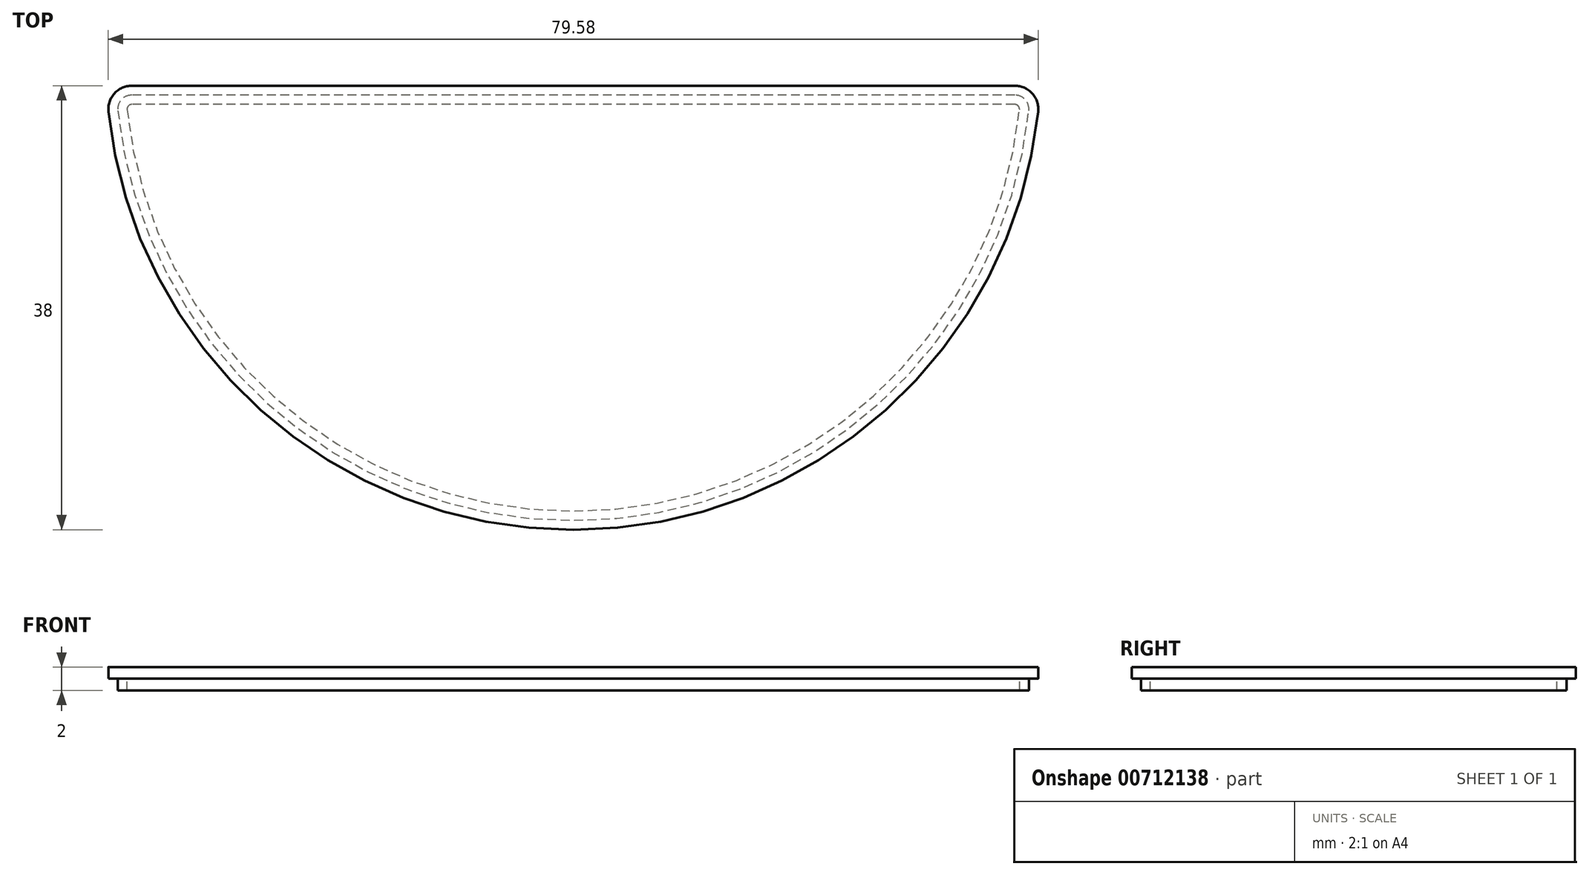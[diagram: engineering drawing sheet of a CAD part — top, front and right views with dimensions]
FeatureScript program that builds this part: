
annotation { "Feature Type Name" : "Feature", "Feature Type Description" : "" }
export const myFeature = defineFeature(function(context is Context, id is Id, definition is map)
    precondition{}
    {
        {
            var Q0;
            Q0=qCreatedBy(makeId("Top.planeOp"),FACE);
            var sketch = newSketch(context, id + "F0", { "sketchPlane" : qUnion([Q0])});
            skLineSegment(sketch, "E0.top", {"start": v(26.52, -2) * mm, "end": v(-49.06, -2) * mm});
            skPoint(sketch, "E1.visualSharp", {"position": v(28.68, -2) * mm});
            skArc(sketch, "E1.filletArc", {"start": v(28.5, -4.21) * mm, "mid": v(28, -2.66) * mm, "end": v(26.52, -2) * mm});
            skArc(sketch, "E2.1", {"start": v(27.71, -4.13) * mm, "mid": v(27.41, -3.2) * mm, "end": v(26.52, -2.8) * mm});
            skLineSegment(sketch, "E2.2", {"start": v(26.52, -2.8) * mm, "end": v(-49.06, -2.8) * mm});
            skArc(sketch, "E3", {"start": v(-51.05, -4.21) * mm, "mid": v(-11.27, -40) * mm, "end": v(28.5, -4.21) * mm});
            skArc(sketch, "E4", {"start": v(-50.25, -4.13) * mm, "mid": v(-11.27, -39.2) * mm, "end": v(27.71, -4.13) * mm});
            skPoint(sketch, "E5.visualSharp", {"position": v(-51.22, -2) * mm});
            skArc(sketch, "E5.filletArc", {"start": v(-49.06, -2) * mm, "mid": v(-50.55, -2.66) * mm, "end": v(-51.05, -4.21) * mm});
            skPoint(sketch, "E6.visualSharp", {"position": v(-50.37, -2.8) * mm});
            skArc(sketch, "E6.filletArc", {"start": v(-49.06, -2.8) * mm, "mid": v(-49.95, -3.2) * mm, "end": v(-50.25, -4.13) * mm});
            skLineSegment(sketch, "E7.0", {"start": v(26.52, -3.6) * mm, "end": v(-49.06, -3.6) * mm});
            skArc(sketch, "E7.1", {"start": v(26.92, -4.04) * mm, "mid": v(26.82, -3.73) * mm, "end": v(26.52, -3.6) * mm});
            skArc(sketch, "E7.2", {"start": v(-49.46, -4.04) * mm, "mid": v(-11.27, -38.4) * mm, "end": v(26.92, -4.04) * mm});
            skArc(sketch, "E7.3", {"start": v(-49.06, -3.6) * mm, "mid": v(-49.36, -3.73) * mm, "end": v(-49.46, -4.04) * mm});
            skSolve(sketch);
        }
        {
            var Q0;
            Q0 = qSketchRegion(id + "F0", true);
            var Q1;
            Q1=makeQuery(id+"F0.imprint","IMPRINT",FACE,{"disambiguationData":[TD([[makeQuery(id+"F0.imprint","IMPRINT",EDGE,{"derivedFrom":sQuery(id+"F0.wireOp",EDGE,"E7.0")}),1.0]])]});
            var Q2;
            Q2=makeQuery(id+"F0.imprint","IMPRINT",FACE,{"disambiguationData":[TD([[makeQuery(id+"F0.imprint","IMPRINT",EDGE,{"derivedFrom":sQuery(id+"F0.wireOp",EDGE,"E2.1")}),1.0]])]});
            extrude(context, id + "F1", {"entities" : qUnion([Q0, Q1, Q2]), "depth" : 1 * mm, "offsetDistance" : 25 * mm});
        }
        {
            var Q0;
            Q0=makeQuery(id+"F0.imprint","IMPRINT",FACE,{"disambiguationData":[TD([[makeQuery(id+"F0.imprint","IMPRINT",EDGE,{"derivedFrom":sQuery(id+"F0.wireOp",EDGE,"E2.1")}),1.0]])]});
            extrude(context, id + "F2", {"entities" : qUnion([Q0]), "operationType" : NewBodyOperationType.ADD, "oppositeDirection" : true, "depth" : 1 * mm, "offsetDistance" : 25 * mm});
        }
    });
